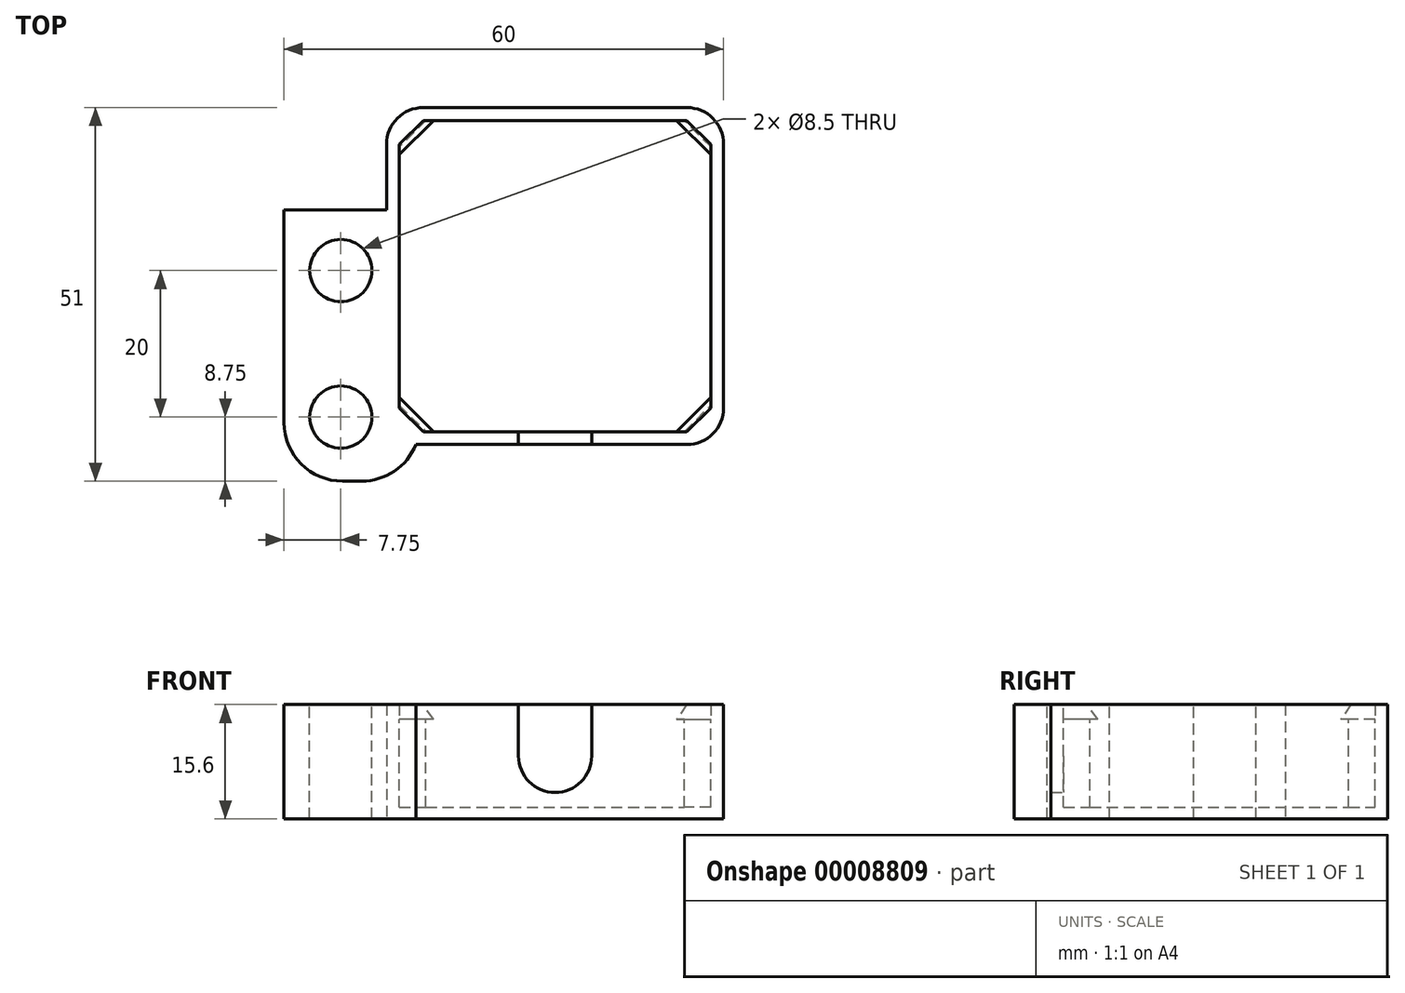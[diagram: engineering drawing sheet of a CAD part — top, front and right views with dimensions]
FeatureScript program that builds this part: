
annotation { "Feature Type Name" : "Feature", "Feature Type Description" : "" }
export const myFeature = defineFeature(function(context is Context, id is Id, definition is map)
    precondition{}
    {
        {
            var Q0;
            Q0=qCreatedBy(makeId("Top.planeOp"),FACE);
            var sketch = newSketch(context, id + "F0", { "sketchPlane" : qUnion([Q0])});
            skLineSegment(sketch, "E0.bottom", {"start": v(-23, 23) * mm, "end": v(23, 23) * mm});
            skLineSegment(sketch, "E0.top", {"start": v(-23, -23) * mm, "end": v(23, -23) * mm});
            skLineSegment(sketch, "E0.left", {"start": v(-23, 23) * mm, "end": v(-23, -23) * mm});
            skLineSegment(sketch, "E0.right", {"start": v(23, 23) * mm, "end": v(23, -23) * mm});
            skLineSegment(sketch, "E1", {"start": v(-23, 23) * mm, "end": v(23, -23) * mm, "construction": true});
            skLineSegment(sketch, "E2", {"start": v(23, 23) * mm, "end": v(-23, -23) * mm, "construction": true});
            skSolve(sketch);
        }
        {
            var Q0;
            Q0=makeQuery(id+"F0.imprint","IMPRINT",FACE,{"disambiguationData":[TD([[makeQuery(id+"F0.imprint","IMPRINT",EDGE,{"derivedFrom":sQuery(id+"F0.wireOp",EDGE,"E0.bottom")}),-1.0]])]});
            extrude(context, id + "F1", {"entities" : qUnion([Q0]), "depth" : 15.6 * mm});
        }
        {
            var Q0;
            Q0=makeQuery(id+"F1.opExtrude","CAP_FACE",FACE,{"disambiguationData":[OSD([sQuery(id+"F0.wireOp",EDGE,"E0.bottom"),sQuery(id+"F0.wireOp",EDGE,"E0.top"),sQuery(id+"F0.wireOp",EDGE,"E0.left"),sQuery(id+"F0.wireOp",EDGE,"E0.right")])],"isStart":false});
            var sketch = newSketch(context, id + "F2", { "sketchPlane" : qUnion([Q0])});
            skLineSegment(sketch, "E3", {"start": v(-17.64, 21.25) * mm, "end": v(17.64, 21.25) * mm});
            skLineSegment(sketch, "E4", {"start": v(17.64, 21.25) * mm, "end": v(21.25, 17.64) * mm});
            skLineSegment(sketch, "E5", {"start": v(21.25, 17.64) * mm, "end": v(21.25, -17.64) * mm});
            skLineSegment(sketch, "E6", {"start": v(21.25, -17.64) * mm, "end": v(17.64, -21.25) * mm});
            skLineSegment(sketch, "E7", {"start": v(17.64, -21.25) * mm, "end": v(-17.64, -21.25) * mm});
            skLineSegment(sketch, "E8", {"start": v(-17.64, -21.25) * mm, "end": v(-21.25, -17.64) * mm});
            skLineSegment(sketch, "E9", {"start": v(-21.25, -17.64) * mm, "end": v(-21.25, 17.64) * mm});
            skLineSegment(sketch, "E10", {"start": v(-21.25, 17.64) * mm, "end": v(-17.64, 21.25) * mm});
            skLineSegment(sketch, "E11", {"start": v(-17.64, 21.25) * mm, "end": v(21.25, -17.64) * mm, "construction": true});
            skLineSegment(sketch, "E12", {"start": v(17.64, -21.25) * mm, "end": v(-21.25, 17.64) * mm, "construction": true});
            skLineSegment(sketch, "E13", {"start": v(17.64, 21.25) * mm, "end": v(-21.25, -17.64) * mm, "construction": true});
            skLineSegment(sketch, "E14", {"start": v(-17.64, -21.25) * mm, "end": v(21.25, 17.64) * mm, "construction": true});
            skLineSegment(sketch, "E15", {"start": v(-21.25, 0) * mm, "end": v(21.25, 0) * mm, "construction": true});
            skSolve(sketch);
        }
        {
            var Q0;
            Q0=makeQuery(id+"F2.imprint","IMPRINT",FACE,{"disambiguationData":[TD([[makeQuery(id+"F2.imprint","IMPRINT",EDGE,{"derivedFrom":sQuery(id+"F2.wireOp",EDGE,"E3")}),-1.0]])]});
            extrude(context, id + "F3", {"entities" : qUnion([Q0]), "operationType" : NewBodyOperationType.REMOVE, "oppositeDirection" : true, "depth" : 14 * mm});
        }
        {
            var Q0;
            Q0=makeQuery(id+"F1.opExtrude","CAP_FACE",FACE,{"disambiguationData":[OSD([sQuery(id+"F0.wireOp",EDGE,"E0.bottom"),sQuery(id+"F0.wireOp",EDGE,"E0.top"),sQuery(id+"F0.wireOp",EDGE,"E0.left"),sQuery(id+"F0.wireOp",EDGE,"E0.right")])],"isStart":false});
            var sketch = newSketch(context, id + "F4", { "sketchPlane" : qUnion([Q0])});
            skLineSegment(sketch, "E16", {"start": v(-16.58, 21.25) * mm, "end": v(16.58, 21.25) * mm});
            skLineSegment(sketch, "E17", {"start": v(16.58, 21.25) * mm, "end": v(21.25, 16.58) * mm});
            skLineSegment(sketch, "E18", {"start": v(21.25, 16.58) * mm, "end": v(21.25, -16.58) * mm});
            skLineSegment(sketch, "E19", {"start": v(21.25, -16.58) * mm, "end": v(16.58, -21.25) * mm});
            skLineSegment(sketch, "E20", {"start": v(16.58, -21.25) * mm, "end": v(-16.58, -21.25) * mm});
            skLineSegment(sketch, "E21", {"start": v(-16.58, -21.25) * mm, "end": v(-21.25, -16.58) * mm});
            skLineSegment(sketch, "E22", {"start": v(-21.25, -16.58) * mm, "end": v(-21.25, 16.58) * mm});
            skLineSegment(sketch, "E23", {"start": v(-21.25, 16.58) * mm, "end": v(-16.58, 21.25) * mm});
            skLineSegment(sketch, "E24", {"start": v(0, 21.25) * mm, "end": v(0, -21.25) * mm, "construction": true});
            skLineSegment(sketch, "E25", {"start": v(21.25, 0) * mm, "end": v(-21.25, 0) * mm, "construction": true});
            skLineSegment(sketch, "E26.bottom", {"start": v(-23, 23) * mm, "end": v(23, 23) * mm, "construction": true});
            skLineSegment(sketch, "E26.top", {"start": v(-23, -23) * mm, "end": v(23, -23) * mm, "construction": true});
            skLineSegment(sketch, "E26.left", {"start": v(-23, 23) * mm, "end": v(-23, -23) * mm, "construction": true});
            skLineSegment(sketch, "E26.right", {"start": v(23, 23) * mm, "end": v(23, -23) * mm, "construction": true});
            skLineSegment(sketch, "E27.bottom", {"start": v(23, 23) * mm, "end": v(-23, 23) * mm});
            skLineSegment(sketch, "E27.top", {"start": v(23, -23) * mm, "end": v(-23, -23) * mm});
            skLineSegment(sketch, "E27.left", {"start": v(23, 23) * mm, "end": v(23, -23) * mm});
            skLineSegment(sketch, "E27.right", {"start": v(-23, 23) * mm, "end": v(-23, -23) * mm});
            skSolve(sketch);
        }
        {
            var Q0;
            Q0=qSketchRegion(id+"F4",true);
            extrude(context, id + "F5", {"entities" : qUnion([Q0]), "operationType" : NewBodyOperationType.ADD, "oppositeDirection" : true, "depth" : 2 * mm});
        }
        {
            var Q0;
            Q0=makeQuery(id+"F5.opExtrude","CAP_EDGE",EDGE,{"disambiguationData":[OSD([sQuery(id+"F4.wireOp",EDGE,"E17")])],"isStart":true});
            var Q1;
            Q1=makeQuery(id+"F5.opExtrude","CAP_EDGE",EDGE,{"disambiguationData":[OSD([sQuery(id+"F4.wireOp",EDGE,"E23")])],"isStart":true});
            var Q2;
            Q2=makeQuery(id+"F5.opExtrude","CAP_EDGE",EDGE,{"disambiguationData":[OSD([sQuery(id+"F4.wireOp",EDGE,"E21")])],"isStart":true});
            var Q3;
            Q3=makeQuery(id+"F5.opExtrude","CAP_EDGE",EDGE,{"disambiguationData":[OSD([sQuery(id+"F4.wireOp",EDGE,"E19")])],"isStart":true});
            chamfer(context, id + "F6", {"entities" : qUnion([Q0, Q1, Q2, Q3]), "chamferType" : ChamferType.TWO_OFFSETS, "width1" : 1 * mm, "oppositeDirection" : false, "width2" : 2 * mm, "tangentPropagation" : true});
        }
        {
            var Q0;
            Q0=makeQuery(id+"F1.opExtrude","SWEPT_EDGE",EDGE,{"disambiguationData":[OSD([sQuery(id+"F0.wireOp",EDGE,"E0.top"),sQuery(id+"F0.wireOp",EDGE,"E0.right")])]});
            var Q1;
            Q1=makeQuery(id+"F1.opExtrude","SWEPT_EDGE",EDGE,{"disambiguationData":[OSD([sQuery(id+"F0.wireOp",EDGE,"E0.bottom"),sQuery(id+"F0.wireOp",EDGE,"E0.right")])]});
            var Q2;
            Q2=makeQuery(id+"F1.opExtrude","SWEPT_EDGE",EDGE,{"disambiguationData":[OSD([sQuery(id+"F0.wireOp",EDGE,"E0.bottom"),sQuery(id+"F0.wireOp",EDGE,"E0.left")])]});
            fillet(context, id + "F7", {"entities" : qUnion([Q0, Q1, Q2]), "radius" : 5 * mm, "tangentPropagation" : true, "allowEdgeOverflow" : false});
        }
        {
            var Q0;
            Q0=makeQuery(id+"F1.opExtrude","SWEPT_FACE",FACE,{"disambiguationData":[OSD([sQuery(id+"F0.wireOp",EDGE,"E0.top")])]});
            var sketch = newSketch(context, id + "F8", { "sketchPlane" : qUnion([Q0])});
            skLineSegment(sketch, "E28.bottom", {"start": v(-5, 15.6) * mm, "end": v(5, 15.6) * mm});
            skLineSegment(sketch, "E28.top", {"start": v(-5, 3.6) * mm, "end": v(5, 3.6) * mm});
            skLineSegment(sketch, "E28.left", {"start": v(-5, 15.6) * mm, "end": v(-5, 3.6) * mm});
            skLineSegment(sketch, "E28.right", {"start": v(5, 15.6) * mm, "end": v(5, 3.6) * mm});
            skSolve(sketch);
        }
        {
            var Q0;
            Q0=makeQuery(id+"F8.imprint","IMPRINT",FACE,{"disambiguationData":[TD([[makeQuery(id+"F8.imprint","IMPRINT",EDGE,{"derivedFrom":sQuery(id+"F8.wireOp",EDGE,"E28.bottom")}),-1.0]])]});
            extrude(context, id + "F9", {"entities" : qUnion([Q0]), "operationType" : NewBodyOperationType.REMOVE, "oppositeDirection" : true, "depth" : 25 * mm});
        }
        {
            var Q0;
            Q0=makeQuery(id+"F9.boolean.opBoolean","COPY",EDGE,{"derivedFrom":makeQuery(id+"F9.opExtrude","SWEPT_EDGE",EDGE,{"disambiguationData":[OSD([sQuery(id+"F0.wireOp",EDGE,"E0.top"),sQuery(id+"F8.wireOp",EDGE,"E28.bottom"),sQuery(id+"F8.wireOp",EDGE,"E28.left")])]})});
            var Q1;
            Q1=makeQuery(id+"F9.boolean.opBoolean","COPY",EDGE,{"derivedFrom":makeQuery(id+"F9.opExtrude","SWEPT_EDGE",EDGE,{"disambiguationData":[OSD([sQuery(id+"F0.wireOp",EDGE,"E0.top"),sQuery(id+"F8.wireOp",EDGE,"E28.bottom"),sQuery(id+"F8.wireOp",EDGE,"E28.right")])]})});
            var Q2;
            Q2=makeQuery(id+"F9.boolean.opBoolean","COPY",EDGE,{"derivedFrom":makeQuery(id+"F9.opExtrude","SWEPT_EDGE",EDGE,{"disambiguationData":[OSD([sQuery(id+"F8.wireOp",EDGE,"E28.top"),sQuery(id+"F8.wireOp",EDGE,"E28.left")])]})});
            var Q3;
            Q3=makeQuery(id+"F9.boolean.opBoolean","COPY",EDGE,{"derivedFrom":makeQuery(id+"F9.opExtrude","SWEPT_EDGE",EDGE,{"disambiguationData":[OSD([sQuery(id+"F8.wireOp",EDGE,"E28.top"),sQuery(id+"F8.wireOp",EDGE,"E28.right")])]})});
            fillet(context, id + "F10", {"entities" : qUnion([Q0, Q1, Q2, Q3]), "radius" : 5 * mm, "tangentPropagation" : true, "allowEdgeOverflow" : false});
        }
        {
            var Q0;
            Q0=makeQuery(id+"F1.opExtrude","SWEPT_FACE",FACE,{"disambiguationData":[OSD([sQuery(id+"F0.wireOp",EDGE,"E0.left")])]});
            extrude(context, id + "F11", {"entities" : qUnion([Q0]), "operationType" : NewBodyOperationType.ADD, "depth" : 14 * mm});
        }
        {
            var Q0;
            {var subQ0=sQuery(id+"F0.wireOp",EDGE,"E0.top");Q0=makeQuery(id+"F11.boolean.opBoolean","MERGE",FACE,{"derivedFrom":[makeQuery(id+"F1.opExtrude","SWEPT_FACE",FACE,{"disambiguationData":[OSD([subQ0])]}),makeQuery(id+"F11.opExtrude","SWEPT_FACE",FACE,{"disambiguationData":[OSD([subQ0,sQuery(id+"F0.wireOp",EDGE,"E0.left")])]})]});}
            var sketch = newSketch(context, id + "F12", { "sketchPlane" : qUnion([Q0])});
            skLineSegment(sketch, "E29.bottom", {"start": v(-37, 15.6) * mm, "end": v(-19, 15.6) * mm});
            skLineSegment(sketch, "E29.top", {"start": v(-37, 0) * mm, "end": v(-19, 0) * mm});
            skLineSegment(sketch, "E29.left", {"start": v(-37, 15.6) * mm, "end": v(-37, 0) * mm});
            skLineSegment(sketch, "E29.right", {"start": v(-19, 15.6) * mm, "end": v(-19, 0) * mm});
            skSolve(sketch);
        }
        {
            var Q0;
            Q0=makeQuery(id+"F12.imprint","IMPRINT",FACE,{"disambiguationData":[TD([[makeQuery(id+"F12.imprint","IMPRINT",EDGE,{"derivedFrom":sQuery(id+"F12.wireOp",EDGE,"E29.bottom")}),-1.0]])]});
            extrude(context, id + "F13", {"entities" : qUnion([Q0]), "operationType" : NewBodyOperationType.ADD, "depth" : 5 * mm});
        }
        {
            var Q0;
            {var subQ0=sQuery(id+"F0.wireOp",EDGE,"E0.left");Q0=makeQuery(id+"F13.boolean.opBoolean","MERGE",FACE,{"derivedFrom":[makeQuery(id+"F11.boolean.opBoolean","MERGE",FACE,{"derivedFrom":[makeQuery(id+"F5.boolean.opBoolean","MERGE",FACE,{"derivedFrom":[makeQuery(id+"F1.opExtrude","CAP_FACE",FACE,{"disambiguationData":[OSD([sQuery(id+"F0.wireOp",EDGE,"E0.bottom"),sQuery(id+"F0.wireOp",EDGE,"E0.top"),subQ0,sQuery(id+"F0.wireOp",EDGE,"E0.right")])],"isStart":false}),makeQuery(id+"F5.opExtrude","CAP_FACE",FACE,{"disambiguationData":[OSD([sQuery(id+"F4.wireOp",EDGE,"E16"),sQuery(id+"F4.wireOp",EDGE,"E17"),sQuery(id+"F4.wireOp",EDGE,"E18"),sQuery(id+"F4.wireOp",EDGE,"E19"),sQuery(id+"F4.wireOp",EDGE,"E20"),sQuery(id+"F4.wireOp",EDGE,"E21"),sQuery(id+"F4.wireOp",EDGE,"E22"),sQuery(id+"F4.wireOp",EDGE,"E23"),sQuery(id+"F4.wireOp",EDGE,"E27.bottom"),sQuery(id+"F4.wireOp",EDGE,"E27.top"),sQuery(id+"F4.wireOp",EDGE,"E27.left"),sQuery(id+"F4.wireOp",EDGE,"E27.right")])],"isStart":true})]}),makeQuery(id+"F11.opExtrude","SWEPT_FACE",FACE,{"disambiguationData":[OSD([subQ0]),TDD([makeQuery(id+"F1.opExtrude","CAP_EDGE",EDGE,{"disambiguationData":[OSD([subQ0])],"isStart":false})])]})]}),makeQuery(id+"F13.opExtrude","SWEPT_FACE",FACE,{"disambiguationData":[OSD([sQuery(id+"F12.wireOp",EDGE,"E29.bottom")])]})]});}
            var sketch = newSketch(context, id + "F14", { "sketchPlane" : qUnion([Q0])});
            skLineSegment(sketch, "E30", {"start": v(-29.25, -51.71) * mm, "end": v(-29.25, 21.52) * mm, "construction": true});
            skCircle(sketch, "E31", {"center": v(-29.25, 0.75) * mm, "radius": 4.25 * mm});
            skCircle(sketch, "E32", {"center": v(-29.25, -19.25) * mm, "radius": 4.25 * mm});
            skSolve(sketch);
        }
        {
            var Q0;
            Q0 = qSketchRegion(id + "F14", true);
            extrude(context, id + "F15", {"entities" : qUnion([Q0]), "operationType" : NewBodyOperationType.REMOVE, "oppositeDirection" : true, "depth" : 25 * mm});
        }
        {
            var Q0;
            Q0=makeQuery(id+"F11.opExtrude","SWEPT_FACE",FACE,{"disambiguationData":[OSD([sQuery(id+"F0.wireOp",EDGE,"E0.bottom"),sQuery(id+"F0.wireOp",EDGE,"E0.left")])]});
            extrude(context, id + "F16", {"entities" : qUnion([Q0]), "operationType" : NewBodyOperationType.REMOVE, "oppositeDirection" : true, "depth" : 9 * mm});
        }
        {
            var Q0;
            {var subQ0=sQuery(id+"F0.wireOp",EDGE,"E0.bottom");var subQ1=sQuery(id+"F0.wireOp",EDGE,"E0.left");Q0=makeQuery(id+"F16.boolean.opBoolean","COPY",EDGE,{"derivedFrom":makeQuery(id+"F16.opExtrude","CAP_EDGE",EDGE,{"disambiguationData":[OSD([subQ0,subQ1]),TDD([makeQuery(id+"F11.opExtrude","CAP_EDGE",EDGE,{"disambiguationData":[OSD([subQ0,subQ1])],"isStart":false})])],"isStart":false})});}
            var Q1;
            Q1=makeQuery(id+"F13.opExtrude","CAP_EDGE",EDGE,{"disambiguationData":[OSD([sQuery(id+"F12.wireOp",EDGE,"E29.left")])],"isStart":false});
            var Q2;
            Q2=makeQuery(id+"F13.opExtrude","CAP_EDGE",EDGE,{"disambiguationData":[OSD([sQuery(id+"F12.wireOp",EDGE,"E29.right")])],"isStart":false});
            fillet(context, id + "F17", {"entities" : qUnion([Q0, Q1, Q2]), "radius" : 8 * mm, "tangentPropagation" : true, "allowEdgeOverflow" : false});
        }
    });
